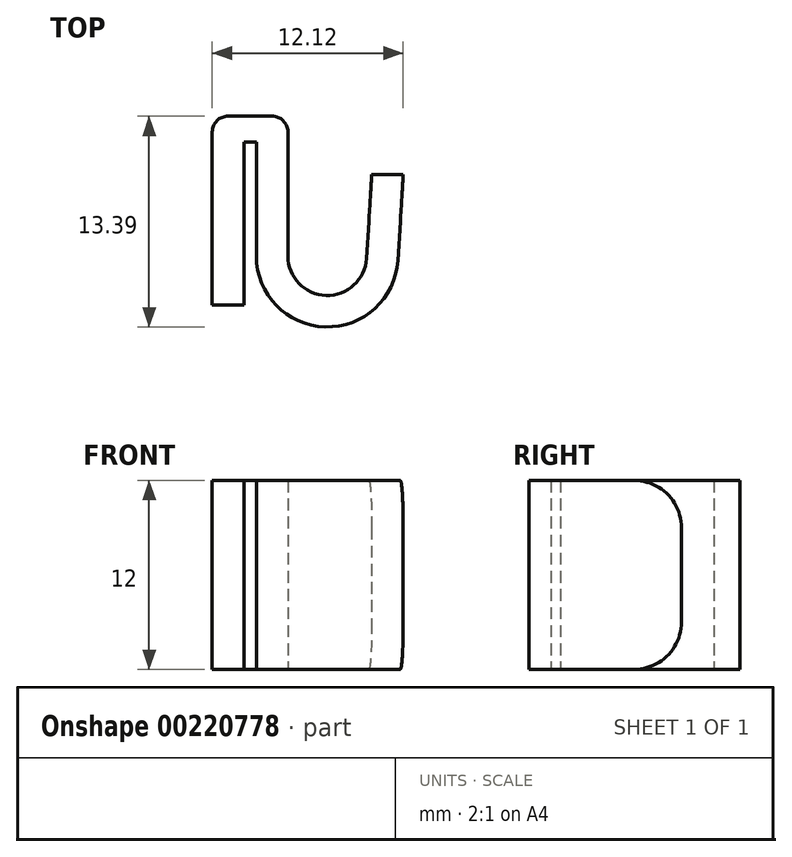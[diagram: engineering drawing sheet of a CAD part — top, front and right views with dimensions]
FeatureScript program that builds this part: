
annotation { "Feature Type Name" : "Feature", "Feature Type Description" : "" }
export const myFeature = defineFeature(function(context is Context, id is Id, definition is map)
    precondition{}
    {
        {
            var Q0;
            Q0=qCreatedBy(makeId("Top.planeOp"),FACE);
            var sketch = newSketch(context, id + "F0", { "sketchPlane" : qUnion([Q0])});
            skLineSegment(sketch, "E0", {"start": v(0, 0) * mm, "end": v(0, 12) * mm});
            skLineSegment(sketch, "E1", {"start": v(0, 12) * mm, "end": v(4.8, 12) * mm});
            skLineSegment(sketch, "E2", {"start": v(4.8, 12) * mm, "end": v(4.8, 0) * mm});
            skLineSegment(sketch, "E3", {"start": v(4.8, 0) * mm, "end": v(2.8, 0) * mm});
            skLineSegment(sketch, "E4", {"start": v(2.8, 0) * mm, "end": v(2.8, 10.35) * mm});
            skLineSegment(sketch, "E5", {"start": v(2.8, 10.35) * mm, "end": v(2, 10.35) * mm});
            skLineSegment(sketch, "E6", {"start": v(2, 10.35) * mm, "end": v(2, 0) * mm});
            skLineSegment(sketch, "E7", {"start": v(2, 0) * mm, "end": v(0, 0) * mm});
            skCircle(sketch, "E8", {"center": v(7.3, 3.11) * mm, "radius": 2.5 * mm});
            skCircle(sketch, "E9", {"center": v(7.3, 3.11) * mm, "radius": 4.5 * mm});
            skLineSegment(sketch, "E10", {"start": v(9.8, 2.96) * mm, "end": v(10.12, 8.3) * mm});
            skLineSegment(sketch, "E11", {"start": v(10.12, 8.3) * mm, "end": v(12.12, 8.3) * mm});
            skLineSegment(sketch, "E12", {"start": v(12.12, 8.3) * mm, "end": v(11.8, 2.84) * mm});
            skSolve(sketch);
        }
        {
            var Q0;
            Q0=makeQuery(id+"F0.imprint","IMPRINT",FACE,{"disambiguationData":[TD([[makeQuery(id+"F0.imprint","IMPRINT",EDGE,{"derivedFrom":sQuery(id+"F0.wireOp",EDGE,"E0")}),-1.0]])]});
            var Q1;
            {var subQ0=sQuery(id+"F0.wireOp",EDGE,"E9");var subQ1=sQuery(id+"F0.wireOp",EDGE,"E2");var subQ2=makeQuery(id+"F0.imprint","INTERSECT",VERTEX,{"derivedFrom":[subQ1,subQ0]});Q1=makeQuery(id+"F0.imprint","IMPRINT",FACE,{"disambiguationData":[TD([[makeQuery(id+"F0.imprint","IMPRINT",EDGE,{"disambiguationData":[TD([[subQ2,-1.0]])],"derivedFrom":subQ1}),-1.0]])]});}
            var Q2;
            {var subQ2=sQuery(id+"F0.wireOp",EDGE,"E3");var subQ7=sQuery(id+"F0.wireOp",EDGE,"E2");var subQ9=makeQuery(id+"F0.imprint","INTERSECT",VERTEX,{"derivedFrom":[subQ7,subQ2]});Q2=makeQuery(id+"F0.imprint","IMPRINT",FACE,{"disambiguationData":[TD([[makeQuery(id+"F0.imprint","IMPRINT",EDGE,{"disambiguationData":[TD([[subQ9,1.0]])],"derivedFrom":subQ7}),1.0]])]});}
            var Q3;
            {var subQ4=sQuery(id+"F0.wireOp",EDGE,"E11");Q3=makeQuery(id+"F0.imprint","IMPRINT",FACE,{"disambiguationData":[TD([[makeQuery(id+"F0.imprint","IMPRINT",EDGE,{"derivedFrom":subQ4}),-1.0]])]});}
            extrude(context, id + "F1", {"entities" : qUnion([Q0, Q1, Q2, Q3]), "depth" : 12 * mm});
        }
        {
            var Q0;
            Q0=makeQuery(id+"F1.opExtrude","CAP_EDGE",EDGE,{"disambiguationData":[OSD([sQuery(id+"F0.wireOp",EDGE,"E11")])],"isStart":false});
            var Q1;
            Q1=makeQuery(id+"F1.opExtrude","CAP_EDGE",EDGE,{"disambiguationData":[OSD([sQuery(id+"F0.wireOp",EDGE,"E11")])],"isStart":true});
            fillet(context, id + "F2", {"entities" : qUnion([Q0, Q1]), "radius" : 3 * mm, "tangentPropagation" : true, "allowEdgeOverflow" : false});
        }
        {
            var Q0;
            Q0=makeQuery(id+"F1.opExtrude","SWEPT_EDGE",EDGE,{"disambiguationData":[OSD([sQuery(id+"F0.wireOp",EDGE,"E0"),sQuery(id+"F0.wireOp",EDGE,"E1")])]});
            var Q1;
            Q1=makeQuery(id+"F1.opExtrude","SWEPT_EDGE",EDGE,{"disambiguationData":[OSD([sQuery(id+"F0.wireOp",EDGE,"E1"),sQuery(id+"F0.wireOp",EDGE,"E2")])]});
            fillet(context, id + "F3", {"entities" : qUnion([Q0, Q1]), "radius" : 1 * mm, "tangentPropagation" : true, "allowEdgeOverflow" : false});
        }
    });
